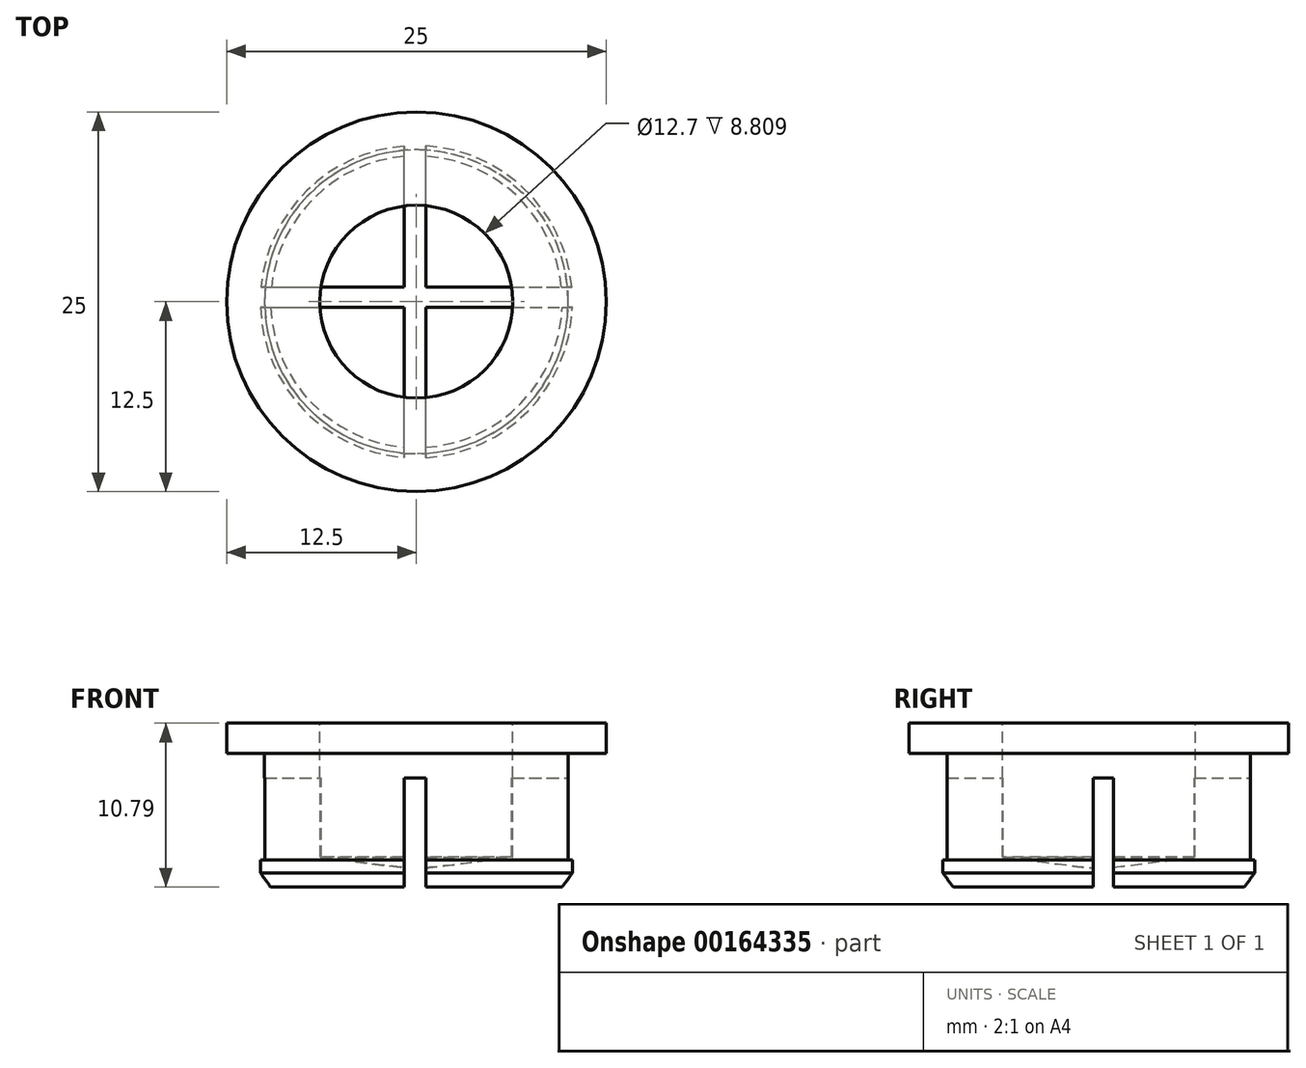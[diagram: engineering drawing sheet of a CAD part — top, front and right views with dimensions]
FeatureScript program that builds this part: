
annotation { "Feature Type Name" : "Feature", "Feature Type Description" : "" }
export const myFeature = defineFeature(function(context is Context, id is Id, definition is map)
    precondition{}
    {
        {
            var Q0;
            Q0=qCreatedBy(makeId("Front.planeOp"),FACE);
            var sketch = newSketch(context, id + "F0", { "sketchPlane" : qUnion([Q0])});
            skLineSegment(sketch, "E0", {"start": v(12.5, 0) * mm, "end": v(12.5, -2) * mm});
            skLineSegment(sketch, "E1", {"start": v(12.5, -2) * mm, "end": v(10, -2) * mm});
            skLineSegment(sketch, "E2", {"start": v(10, -2) * mm, "end": v(10, -9) * mm});
            skLineSegment(sketch, "E3", {"start": v(10, -9) * mm, "end": v(10.28, -9) * mm});
            skLineSegment(sketch, "E4", {"start": v(10.28, -9) * mm, "end": v(10.28, -9.85) * mm});
            skLineSegment(sketch, "E5", {"start": v(10.28, -9.85) * mm, "end": v(9.6, -10.8) * mm});
            skLineSegment(sketch, "E6", {"start": v(9.6, -10.8) * mm, "end": v(0, -10.8) * mm});
            skLineSegment(sketch, "E7", {"start": v(6.35, 0) * mm, "end": v(6.35, -8.8) * mm});
            skLineSegment(sketch, "E8", {"start": v(6.35, -8.8) * mm, "end": v(0, -9.63) * mm});
            skLineSegment(sketch, "E9", {"start": v(0, -9.63) * mm, "end": v(0, -10.8) * mm});
            skLineSegment(sketch, "E10", {"start": v(6.35, 0) * mm, "end": v(12.5, 0) * mm});
            skSolve(sketch);
        }
        {
            var Q0;
            Q0=makeQuery(id+"F0.imprint","IMPRINT",FACE,{"disambiguationData":[TD([[makeQuery(id+"F0.imprint","IMPRINT",EDGE,{"derivedFrom":sQuery(id+"F0.wireOp",EDGE,"E0")}),-1.0]])]});
            var Q1;
            Q1=sQuery(id+"F0.wireOp",EDGE,"E9");
            revolve(context, id + "F1", {"entities" : qUnion([Q0]), "axis" : qUnion([Q1]), "revolveType" : RevolveType.FULL});
        }
        {
            var Q0;
            Q0=makeQuery(id+"F1.opRevolve","SWEPT_FACE",FACE,{"disambiguationData":[OSD([sQuery(id+"F0.wireOp",EDGE,"E6")])]});
            var sketch = newSketch(context, id + "F2", { "sketchPlane" : qUnion([Q0])});
            skLineSegment(sketch, "E11.bottom", {"start": v(-0.82, 10.64) * mm, "end": v(0.61, 10.64) * mm});
            skLineSegment(sketch, "E11.top", {"start": v(-0.82, -11.44) * mm, "end": v(0.61, -11.44) * mm});
            skLineSegment(sketch, "E11.left", {"start": v(-0.82, 10.64) * mm, "end": v(-0.82, -11.44) * mm});
            skLineSegment(sketch, "E11.right", {"start": v(0.61, 10.64) * mm, "end": v(0.61, -11.44) * mm});
            skLineSegment(sketch, "E12.bottom", {"start": v(-10.68, 0.36) * mm, "end": v(11, 0.36) * mm});
            skLineSegment(sketch, "E12.top", {"start": v(-10.68, -0.97) * mm, "end": v(11, -0.97) * mm});
            skLineSegment(sketch, "E12.left", {"start": v(-10.68, 0.36) * mm, "end": v(-10.68, -0.97) * mm});
            skLineSegment(sketch, "E12.right", {"start": v(11, 0.36) * mm, "end": v(11, -0.97) * mm});
            skSolve(sketch);
        }
        {
            var Q0;
            Q0 = qSketchRegion(id + "F2", true);
            extrude(context, id + "F3", {"entities" : qUnion([Q0]), "operationType" : NewBodyOperationType.REMOVE, "flatOperationType" : FlatOperationType.REMOVE, "oppositeDirection" : true, "offsetDistance" : 25 * mm, "depth" : 7.2 * mm, "domain" : OperationDomain.MODEL});
        }
    });
